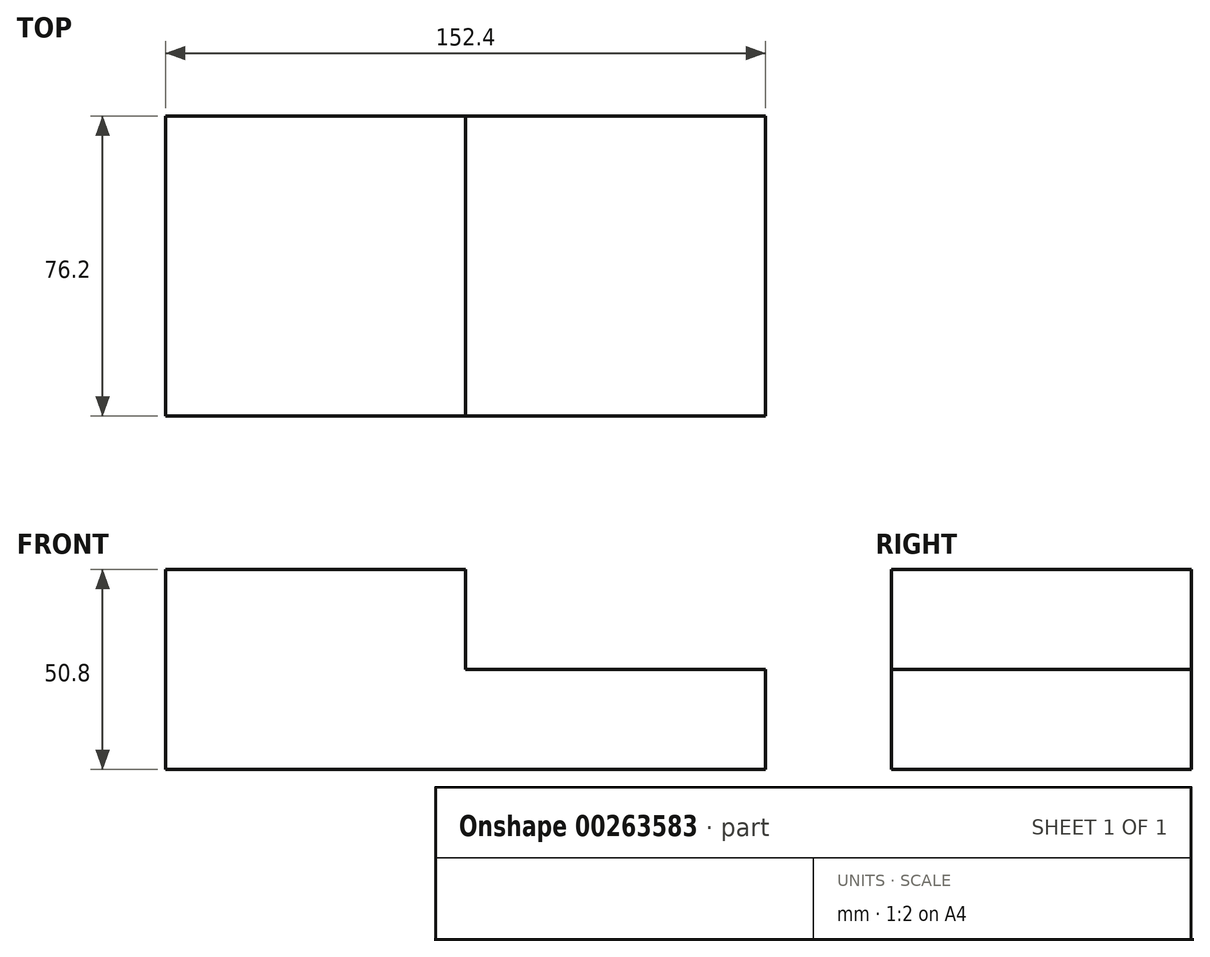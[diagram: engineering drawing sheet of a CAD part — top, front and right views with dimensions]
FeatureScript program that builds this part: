
annotation { "Feature Type Name" : "Feature", "Feature Type Description" : "" }
export const myFeature = defineFeature(function(context is Context, id is Id, definition is map)
    precondition{}
    {
        {
            var Q0;
            Q0=qCreatedBy(makeId("Front.planeOp"),FACE);
            var sketch = newSketch(context, id + "F0", { "sketchPlane" : qUnion([Q0])});
            skLineSegment(sketch, "E0.bottom", {"start": v(-110.76, 0) * mm, "end": v(41.64, 0) * mm});
            skLineSegment(sketch, "E0.top", {"start": v(-34.56, 25.4) * mm, "end": v(41.64, 25.4) * mm});
            skLineSegment(sketch, "E0.left", {"start": v(-110.76, 0) * mm, "end": v(-110.76, 25.4) * mm});
            skLineSegment(sketch, "E0.right", {"start": v(41.64, 0) * mm, "end": v(41.64, 25.4) * mm});
            skLineSegment(sketch, "E1.top", {"start": v(-110.76, 50.8) * mm, "end": v(-34.56, 50.8) * mm});
            skLineSegment(sketch, "E1.left", {"start": v(-110.76, 25.4) * mm, "end": v(-110.76, 50.8) * mm});
            skLineSegment(sketch, "E1.right", {"start": v(-34.56, 25.4) * mm, "end": v(-34.56, 50.8) * mm});
            skSolve(sketch);
        }
        {
            var Q0;
            Q0=makeQuery(id+"F0.imprint","IMPRINT",FACE,{"disambiguationData":[TD([[makeQuery(id+"F0.imprint","IMPRINT",EDGE,{"derivedFrom":sQuery(id+"F0.wireOp",EDGE,"E0.bottom")}),1.0]])]});
            extrude(context, id + "F1", {"entities" : qUnion([Q0]), "depth" : 76.2 * mm});
        }
    });
